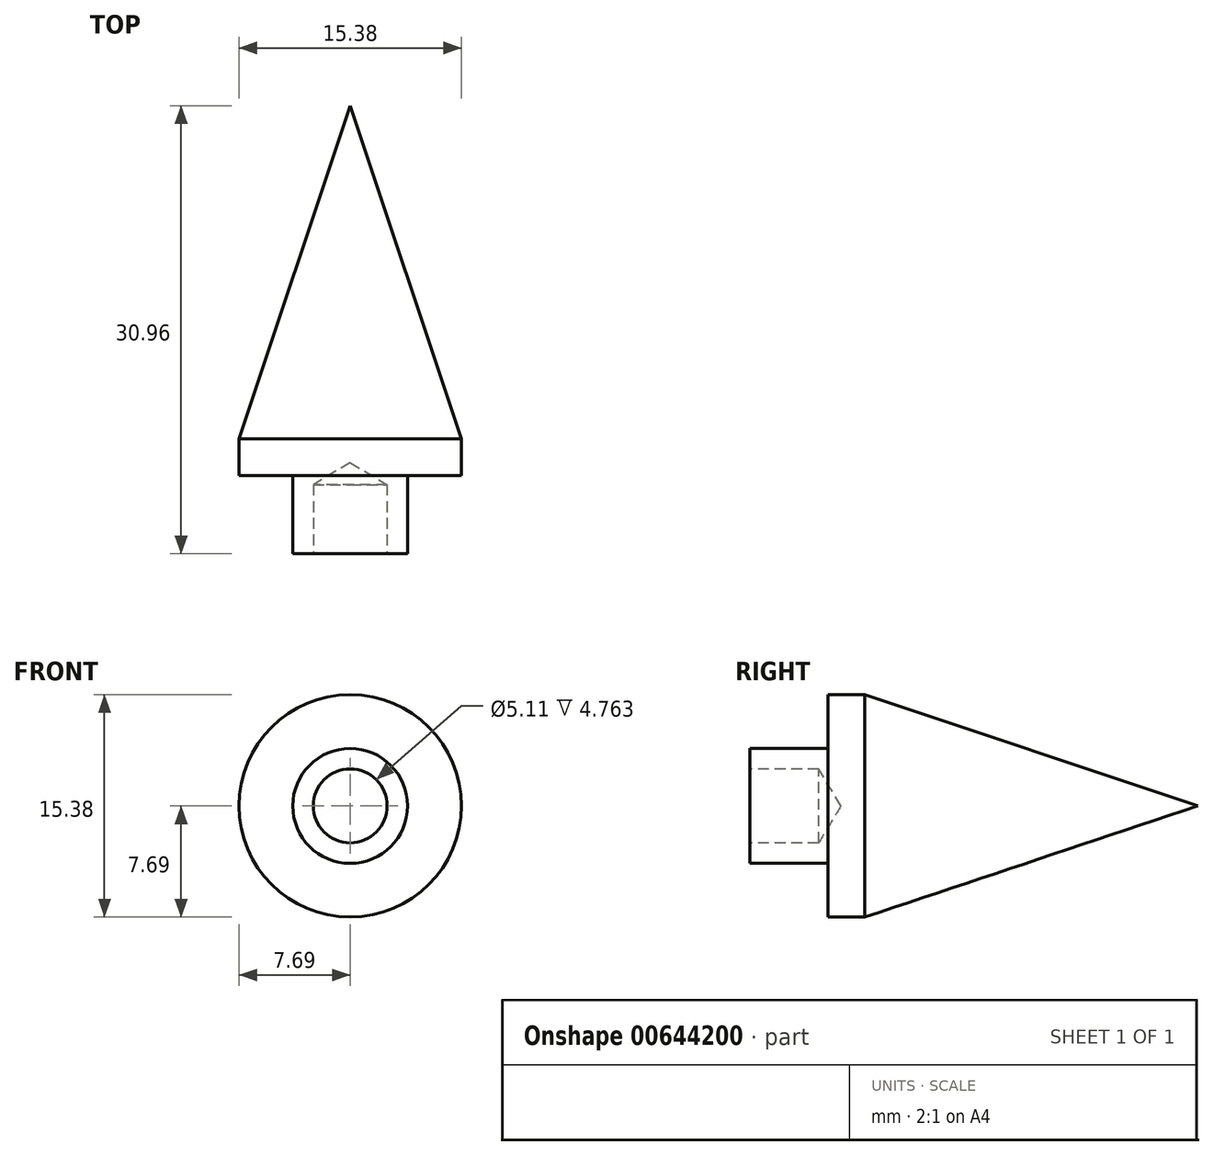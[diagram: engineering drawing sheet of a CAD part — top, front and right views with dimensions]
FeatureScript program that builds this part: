
annotation { "Feature Type Name" : "Feature", "Feature Type Description" : "" }
export const myFeature = defineFeature(function(context is Context, id is Id, definition is map)
    precondition{}
    {
        {
            var Q0;
            Q0=qCreatedBy(makeId("Front.planeOp"),FACE);
            var sketch = newSketch(context, id + "F0", { "sketchPlane" : qUnion([Q0])});
            skCircle(sketch, "E0", {"center": v(0, 0) * mm, "radius": 3.97 * mm});
            skSolve(sketch);
        }
        {
            var Q0;
            Q0=makeQuery(id+"F0.imprint","IMPRINT",FACE,{"disambiguationData":[TD([[makeQuery(id+"F0.imprint","IMPRINT",EDGE,{"derivedFrom":sQuery(id+"F0.wireOp",EDGE,"E0")}),1.0]])]});
            extrude(context, id + "F1", {"entities" : qUnion([Q0]), "depth" : 7.94 * mm, "offsetDistance" : 25.4 * mm});
        }
        {
            var Q0;
            Q0=makeQuery(id+"F1.opExtrude","CAP_FACE",FACE,{"disambiguationData":[OSD([sQuery(id+"F0.wireOp",EDGE,"E0")])],"isStart":false});
            var sketch = newSketch(context, id + "F2", { "sketchPlane" : qUnion([Q0])});
            skPoint(sketch, "E1", {"position": v(0, 0) * mm});
            skSolve(sketch);
        }
        {
            var Q0;
            Q0=sQuery(id+"F2.wireOp",VERTEX,"E1");
            var Q1;
            Q1=makeQuery(id+"F1.opExtrude","SWEPT_BODY",BODY,{"disambiguationData":[OSD([sQuery(id+"F0.wireOp",EDGE,"E0")])]});
            hole(context, id + "F3", {"style" : HoleStyle.SIMPLE, "endStyle" : HoleEndStyle.BLIND, "standardTappedOrClearance" : lookupTablePath({ "standard" : "ANSI", "fit" : "Normal (ASME)", "size" : "#10", "type" : "Clearance" }), "standardBlindInLast" : lookupTablePath({ "fit" : "Free", "standard" : "ANSI", "size" : "#10", "type" : "Clearance" }), "holeDiameter" : 5.1 * mm, "majorDiameter" : 6.35 * mm, "holeDepth" : 4.76 * mm, "isTappedThrough" : true, "tappedDepth" : 12.7 * mm, "tapClearance" : 3, "locations" : qUnion([Q0]), "scope" : qUnion([Q1])});
        }
        {
            var Q0;
            Q0=qCreatedBy(makeId("Right.planeOp"),FACE);
            var sketch = newSketch(context, id + "F4", { "sketchPlane" : qUnion([Q0])});
            skLineSegment(sketch, "E2", {"start": v(0, 0) * mm, "end": v(0, 7.69) * mm});
            skLineSegment(sketch, "E3", {"start": v(0, 7.69) * mm, "end": v(23.02, 0) * mm});
            skLineSegment(sketch, "E4", {"start": v(23.02, 0) * mm, "end": v(0, 0) * mm});
            skSolve(sketch);
        }
        {
            var Q0;
            Q0=makeQuery(id+"F4.imprint","IMPRINT",FACE,{"disambiguationData":[TD([[makeQuery(id+"F4.imprint","IMPRINT",EDGE,{"derivedFrom":sQuery(id+"F4.wireOp",EDGE,"E2")}),-1.0]])]});
            var Q1;
            Q1=sQuery(id+"F4.wireOp",EDGE,"E4");
            revolve(context, id + "F5", {"operationType" : NewBodyOperationType.ADD, "entities" : qUnion([Q0]), "axis" : qUnion([Q1]), "revolveType" : RevolveType.FULL});
        }
        {
            var Q0;
            Q0=makeQuery(id+"F5.opRevolve","SWEPT_FACE",FACE,{"disambiguationData":[OSD([sQuery(id+"F4.wireOp",EDGE,"E2")])]});
            extrude(context, id + "F6", {"entities" : qUnion([Q0]), "operationType" : NewBodyOperationType.ADD, "depth" : 2.54 * mm, "offsetDistance" : 25.4 * mm});
        }
    });
